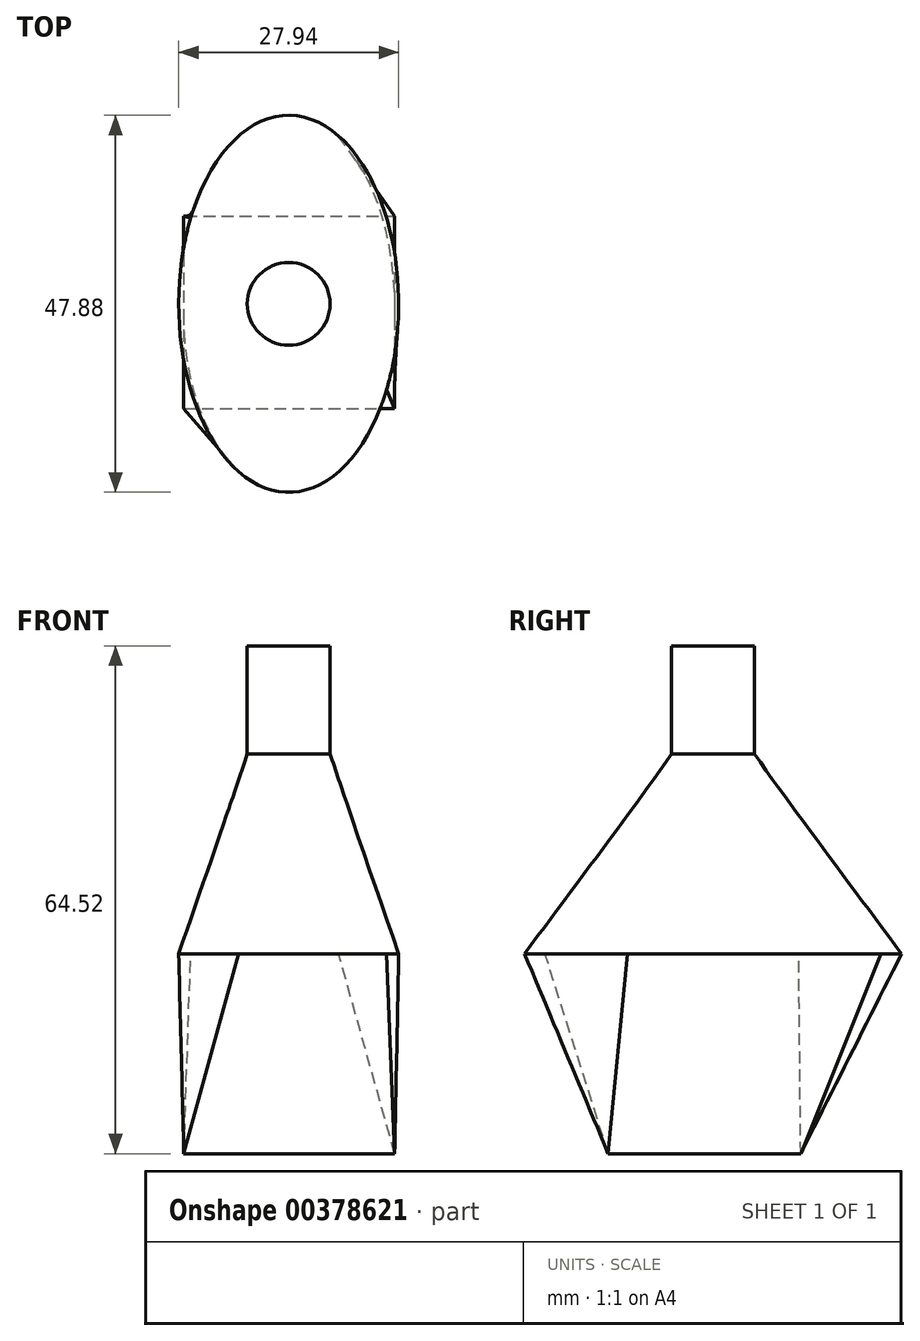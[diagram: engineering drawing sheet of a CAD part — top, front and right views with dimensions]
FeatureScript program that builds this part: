
annotation { "Feature Type Name" : "Feature", "Feature Type Description" : "" }
export const myFeature = defineFeature(function(context is Context, id is Id, definition is map)
    precondition{}
    {
        {
            var Q0;
            Q0=qCreatedBy(makeId("Top.planeOp"),FACE);
            var sketch = newSketch(context, id + "F0", { "sketchPlane" : qUnion([Q0])});
            skLineSegment(sketch, "E0.bottom", {"start": v(-13.32, 11.14) * mm, "end": v(13.48, 11.14) * mm});
            skLineSegment(sketch, "E0.top", {"start": v(-13.32, -13.32) * mm, "end": v(13.48, -13.32) * mm});
            skLineSegment(sketch, "E0.left", {"start": v(-13.32, 11.14) * mm, "end": v(-13.32, -13.32) * mm});
            skLineSegment(sketch, "E0.right", {"start": v(13.48, 11.14) * mm, "end": v(13.48, -13.32) * mm});
            skSolve(sketch);
        }
        {
            var Q0;
            Q0=qCreatedBy(makeId("Top.planeOp"),FACE);
            cPlane(context, id + "F1", {"entities" : qUnion([Q0]), "cplaneType" : CPlaneType.OFFSET, "offset" : 25.4 * mm, "width" : 152.4 * mm, "height" : 152.4 * mm});
        }
        {
            var Q0;
            Q0=qCreatedBy(id+"F1.planeOp",FACE);
            var sketch = newSketch(context, id + "F2", { "sketchPlane" : qUnion([Q0])});
            skEllipse(sketch, "E1", {"center": v(0, 0) * mm, "majorRadius": 23.94 * mm, "minorRadius": 13.97 * mm, "majorAxis": v(0, 1)});
            skSolve(sketch);
        }
        {
            var Q0;
            Q0=qCreatedBy(id+"F1.planeOp",FACE);
            cPlane(context, id + "F3", {"entities" : qUnion([Q0]), "cplaneType" : CPlaneType.OFFSET, "offset" : 25.4 * mm, "width" : 152.4 * mm, "height" : 152.4 * mm});
        }
        {
            var Q0;
            Q0=qCreatedBy(id+"F3.planeOp",FACE);
            var sketch = newSketch(context, id + "F4", { "sketchPlane" : qUnion([Q0])});
            skCircle(sketch, "E2", {"center": v(0, 0) * mm, "radius": 5.26 * mm});
            skSolve(sketch);
        }
        {
            var Q0;
            Q0=makeQuery(id+"F0.imprint","IMPRINT",FACE,{"disambiguationData":[TD([[makeQuery(id+"F0.imprint","IMPRINT",EDGE,{"derivedFrom":sQuery(id+"F0.wireOp",EDGE,"E0.bottom")}),-1.0]])]});
            var Q1;
            Q1=makeQuery(id+"F2.imprint","IMPRINT",FACE,{"disambiguationData":[TD([[makeQuery(id+"F2.imprint","IMPRINT",EDGE,{"derivedFrom":sQuery(id+"F2.wireOp",EDGE,"E1")}),1.0]])]});
            loft(context, id + "F5", {"sheetProfilesArray" : [{ "sheetProfileEntities" : qUnion([Q0]) }, { "sheetProfileEntities" : qUnion([Q1]) }]});
        }
        {
            var Q1;
            Q1=makeQuery(id+"F5.opLoft","CAP_FACE",FACE,{"disambiguationData":[OSD([makeQuery(id+"F2.imprint","IMPRINT",FACE,{"disambiguationData":[TD([[makeQuery(id+"F2.imprint","IMPRINT",EDGE,{"derivedFrom":sQuery(id+"F2.wireOp",EDGE,"E1")}),1.0]])]})])],"isStart":true});
            var Q2;
            Q2=makeQuery(id+"F4.imprint","IMPRINT",FACE,{"disambiguationData":[TD([[makeQuery(id+"F4.imprint","IMPRINT",EDGE,{"derivedFrom":sQuery(id+"F4.wireOp",EDGE,"E2")}),1.0]])]});
            loft(context, id + "F6", {"operationType" : NewBodyOperationType.ADD, "sheetProfilesArray" : [{ "sheetProfileEntities" : qUnion([Q1]) }, { "sheetProfileEntities" : qUnion([Q2]) }]});
        }
        {
            var Q0;
            Q0 = qSketchRegion(id + "F4", true);
            extrude(context, id + "F7", {"entities" : qUnion([Q0]), "depth" : 13.72 * mm});
        }
    });
